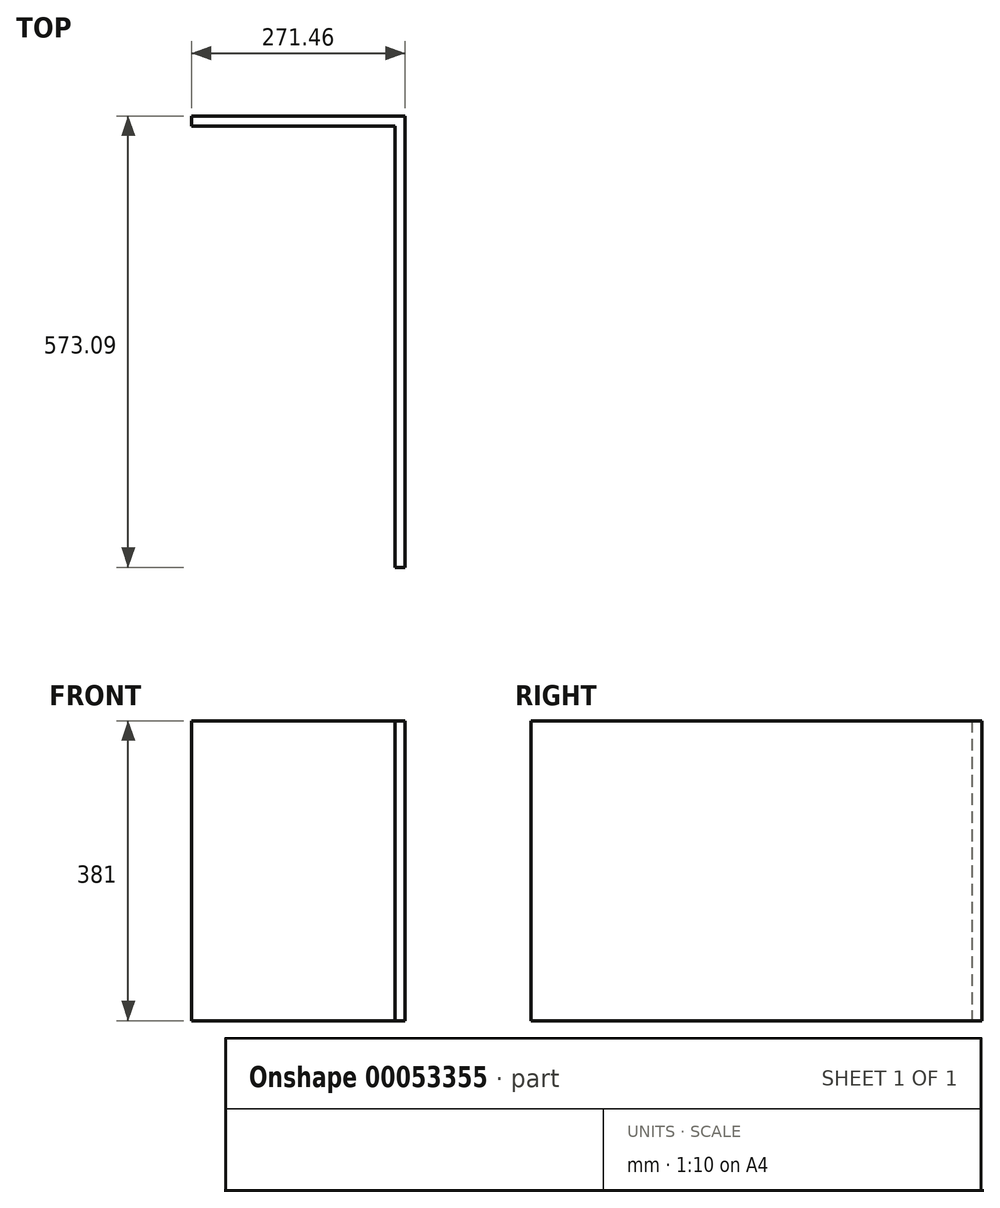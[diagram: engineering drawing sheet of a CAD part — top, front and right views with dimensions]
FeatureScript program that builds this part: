
annotation { "Feature Type Name" : "Feature", "Feature Type Description" : "" }
export const myFeature = defineFeature(function(context is Context, id is Id, definition is map)
    precondition{}
    {
        {
            var Q0;
            Q0=qCreatedBy(makeId("Top.planeOp"),FACE);
            var sketch = newSketch(context, id + "F0", { "sketchPlane" : qUnion([Q0])});
            skLineSegment(sketch, "E0.bottom", {"start": v(-131.64, 280.93) * mm, "end": v(139.82, 280.93) * mm});
            skLineSegment(sketch, "E0.top", {"start": v(-131.64, -292.16) * mm, "end": v(139.82, -292.16) * mm});
            skLineSegment(sketch, "E0.left", {"start": v(-131.64, 280.93) * mm, "end": v(-131.64, -292.16) * mm});
            skLineSegment(sketch, "E0.right", {"start": v(139.82, 280.93) * mm, "end": v(139.82, -292.16) * mm});
            skLineSegment(sketch, "E1.left", {"start": v(-131.64, 280.93) * mm, "end": v(-131.64, 280.93) * mm});
            skLineSegment(sketch, "E1.right", {"start": v(139.82, 280.93) * mm, "end": v(139.82, 280.93) * mm});
            skLineSegment(sketch, "E2", {"start": v(-131.64, 280.93) * mm, "end": v(-131.64, 268.22) * mm});
            skLineSegment(sketch, "E3", {"start": v(-131.64, 268.22) * mm, "end": v(139.82, 268.22) * mm});
            skLineSegment(sketch, "E4", {"start": v(139.82, 280.93) * mm, "end": v(127.12, 280.93) * mm});
            skLineSegment(sketch, "E5", {"start": v(-131.64, 280.93) * mm, "end": v(-118.94, 280.93) * mm});
            skLineSegment(sketch, "E6", {"start": v(-118.94, 280.93) * mm, "end": v(-118.94, -292.16) * mm});
            skLineSegment(sketch, "E7", {"start": v(127.12, 280.93) * mm, "end": v(127.12, -292.16) * mm});
            skSolve(sketch);
        }
        {
            var Q0;
            {var subQ0=sQuery(id+"F0.wireOp",EDGE,"E6");var subQ1=sQuery(id+"F0.wireOp",EDGE,"E0.bottom");var subQ2=makeQuery(id+"F0.imprint","INTERSECT",VERTEX,{"derivedFrom":[subQ1,subQ0]});Q0=makeQuery(id+"F0.imprint","IMPRINT",FACE,{"disambiguationData":[TD([[makeQuery(id+"F0.imprint","IMPRINT",EDGE,{"disambiguationData":[TD([[subQ2,1.0]])],"derivedFrom":subQ1}),-1.0]])]});}
            var Q1;
            {var subQ0=sQuery(id+"F0.wireOp",EDGE,"E6");var subQ1=sQuery(id+"F0.wireOp",EDGE,"E0.bottom");var subQ2=makeQuery(id+"F0.imprint","INTERSECT",VERTEX,{"derivedFrom":[subQ1,subQ0]});Q1=makeQuery(id+"F0.imprint","IMPRINT",FACE,{"disambiguationData":[TD([[makeQuery(id+"F0.imprint","IMPRINT",EDGE,{"disambiguationData":[TD([[subQ2,-1.0]])],"derivedFrom":subQ1}),-1.0]])]});}
            var Q2;
            {var subQ0=sQuery(id+"F0.wireOp",EDGE,"E0.right");var subQ1=sQuery(id+"F0.wireOp",EDGE,"E0.bottom");var subQ2=makeQuery(id+"F0.imprint","INTERSECT",VERTEX,{"derivedFrom":[subQ1,subQ0]});Q2=makeQuery(id+"F0.imprint","IMPRINT",FACE,{"disambiguationData":[TD([[makeQuery(id+"F0.imprint","IMPRINT",EDGE,{"disambiguationData":[TD([[subQ2,1.0]])],"derivedFrom":subQ1}),-1.0]])]});}
            extrude(context, id + "F1", {"entities" : qUnion([Q0, Q1, Q2]), "depth" : 381 * mm, "offsetDistance" : 25.4 * mm});
        }
        {
            var Q0;
            {var subQ0=sQuery(id+"F0.wireOp",EDGE,"E0.right");var subQ1=sQuery(id+"F0.wireOp",EDGE,"E0.bottom");var subQ2=makeQuery(id+"F0.imprint","INTERSECT",VERTEX,{"derivedFrom":[subQ1,subQ0]});Q0=makeQuery(id+"F0.imprint","IMPRINT",FACE,{"disambiguationData":[TD([[makeQuery(id+"F0.imprint","IMPRINT",EDGE,{"disambiguationData":[TD([[subQ2,1.0]])],"derivedFrom":subQ1}),-1.0]])]});}
            var Q1;
            {var subQ0=sQuery(id+"F0.wireOp",EDGE,"E0.right");var subQ1=sQuery(id+"F0.wireOp",EDGE,"E0.top");var subQ2=makeQuery(id+"F0.imprint","INTERSECT",VERTEX,{"derivedFrom":[subQ1,subQ0]});Q1=makeQuery(id+"F0.imprint","IMPRINT",FACE,{"disambiguationData":[TD([[makeQuery(id+"F0.imprint","IMPRINT",EDGE,{"disambiguationData":[TD([[subQ2,1.0]])],"derivedFrom":subQ1}),1.0]])]});}
            extrude(context, id + "F2", {"entities" : qUnion([Q0, Q1]), "operationType" : NewBodyOperationType.ADD, "depth" : 381 * mm, "offsetDistance" : 25.4 * mm});
        }
    });
